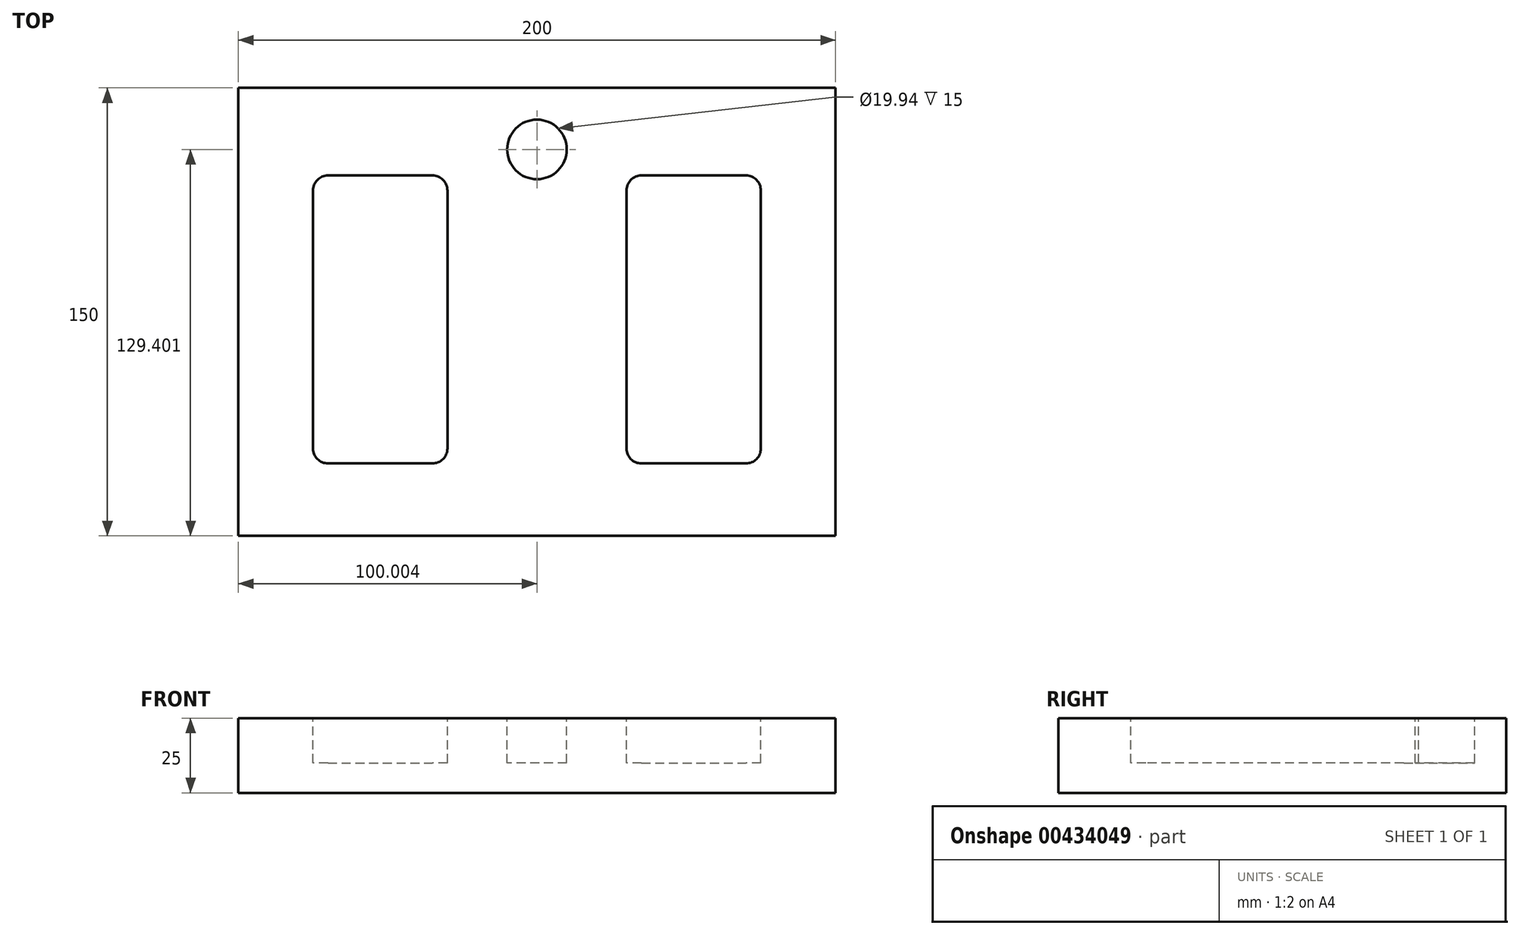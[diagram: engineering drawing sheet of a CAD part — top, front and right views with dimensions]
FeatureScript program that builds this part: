
annotation { "Feature Type Name" : "Feature", "Feature Type Description" : "" }
export const myFeature = defineFeature(function(context is Context, id is Id, definition is map)
    precondition{}
    {
        {
            var Q0;
            Q0=qCreatedBy(makeId("Top.planeOp"),FACE);
            var sketch = newSketch(context, id + "F0", { "sketchPlane" : qUnion([Q0])});
            skLineSegment(sketch, "E0.bottom", {"start": v(-75.08, 74.74) * mm, "end": v(124.92, 74.74) * mm});
            skLineSegment(sketch, "E0.top", {"start": v(-75.08, -75.26) * mm, "end": v(124.92, -75.26) * mm});
            skLineSegment(sketch, "E0.left", {"start": v(-75.08, 74.74) * mm, "end": v(-75.08, -75.26) * mm});
            skLineSegment(sketch, "E0.right", {"start": v(124.92, 74.74) * mm, "end": v(124.92, -75.26) * mm});
            skSolve(sketch);
        }
        {
            var Q0;
            Q0 = qSketchRegion(id + "F0", true);
            extrude(context, id + "F1", {"entities" : qUnion([Q0]), "depth" : 25 * mm});
        }
        {
            var Q0;
            Q0=makeQuery(id+"F1.opExtrude","CAP_FACE",FACE,{"disambiguationData":[OSD([sQuery(id+"F0.wireOp",EDGE,"E0.bottom"),sQuery(id+"F0.wireOp",EDGE,"E0.top"),sQuery(id+"F0.wireOp",EDGE,"E0.left"),sQuery(id+"F0.wireOp",EDGE,"E0.right")])],"isStart":false});
            var sketch = newSketch(context, id + "F2", { "sketchPlane" : qUnion([Q0])});
            skCircle(sketch, "E1", {"center": v(24.92, 54.14) * mm, "radius": 9.97 * mm});
            skSolve(sketch);
        }
        {
            var Q0;
            Q0 = qSketchRegion(id + "F2", true);
            extrude(context, id + "F3", {"entities" : qUnion([Q0]), "operationType" : NewBodyOperationType.REMOVE, "oppositeDirection" : true, "depth" : 15 * mm});
        }
        {
            var Q0;
            Q0=makeQuery(id+"F1.opExtrude","CAP_FACE",FACE,{"disambiguationData":[OSD([sQuery(id+"F0.wireOp",EDGE,"E0.bottom"),sQuery(id+"F0.wireOp",EDGE,"E0.top"),sQuery(id+"F0.wireOp",EDGE,"E0.left"),sQuery(id+"F0.wireOp",EDGE,"E0.right")])],"isStart":false});
            var sketch = newSketch(context, id + "F4", { "sketchPlane" : qUnion([Q0])});
            skLineSegment(sketch, "E2.bottom", {"start": v(-45.08, 45.42) * mm, "end": v(-10.08, 45.42) * mm});
            skLineSegment(sketch, "E2.top", {"start": v(-45.08, -50.99) * mm, "end": v(-10.08, -50.99) * mm});
            skLineSegment(sketch, "E2.left", {"start": v(-50.08, 40.42) * mm, "end": v(-50.08, -45.99) * mm});
            skLineSegment(sketch, "E2.right", {"start": v(-5.08, 40.42) * mm, "end": v(-5.08, -45.99) * mm});
            skLineSegment(sketch, "E3.bottom", {"start": v(59.92, 45.42) * mm, "end": v(94.92, 45.42) * mm});
            skLineSegment(sketch, "E3.top", {"start": v(59.92, -50.99) * mm, "end": v(94.92, -50.99) * mm});
            skLineSegment(sketch, "E3.left", {"start": v(54.92, 40.42) * mm, "end": v(54.92, -45.99) * mm});
            skLineSegment(sketch, "E3.right", {"start": v(99.92, 40.42) * mm, "end": v(99.92, -45.99) * mm});
            skPoint(sketch, "E4.visualSharp", {"position": v(-50.08, 45.42) * mm});
            skArc(sketch, "E4.filletArc", {"start": v(-45.08, 45.42) * mm, "mid": v(-48.61, 43.95) * mm, "end": v(-50.08, 40.42) * mm});
            skPoint(sketch, "E5.visualSharp", {"position": v(-5.08, 45.42) * mm});
            skArc(sketch, "E5.filletArc", {"start": v(-5.08, 40.42) * mm, "mid": v(-6.54, 43.95) * mm, "end": v(-10.08, 45.42) * mm});
            skPoint(sketch, "E6.visualSharp", {"position": v(-5.08, -50.99) * mm});
            skArc(sketch, "E6.filletArc", {"start": v(-10.08, -50.99) * mm, "mid": v(-6.54, -49.52) * mm, "end": v(-5.08, -45.99) * mm});
            skPoint(sketch, "E7.visualSharp", {"position": v(-50.08, -50.99) * mm});
            skArc(sketch, "E7.filletArc", {"start": v(-50.08, -45.99) * mm, "mid": v(-48.61, -49.52) * mm, "end": v(-45.08, -50.99) * mm});
            skPoint(sketch, "E8.visualSharp", {"position": v(54.92, 45.42) * mm});
            skArc(sketch, "E8.filletArc", {"start": v(59.92, 45.42) * mm, "mid": v(56.39, 43.95) * mm, "end": v(54.92, 40.42) * mm});
            skPoint(sketch, "E9.visualSharp", {"position": v(99.92, 45.42) * mm});
            skArc(sketch, "E9.filletArc", {"start": v(99.92, 40.42) * mm, "mid": v(98.46, 43.95) * mm, "end": v(94.92, 45.42) * mm});
            skPoint(sketch, "E10.visualSharp", {"position": v(99.92, -50.99) * mm});
            skArc(sketch, "E10.filletArc", {"start": v(94.92, -50.99) * mm, "mid": v(98.46, -49.52) * mm, "end": v(99.92, -45.99) * mm});
            skPoint(sketch, "E11.visualSharp", {"position": v(54.92, -50.99) * mm});
            skArc(sketch, "E11.filletArc", {"start": v(54.92, -45.99) * mm, "mid": v(56.39, -49.52) * mm, "end": v(59.92, -50.99) * mm});
            skSolve(sketch);
        }
        {
            var Q0;
            Q0 = qSketchRegion(id + "F4", true);
            extrude(context, id + "F5", {"entities" : qUnion([Q0]), "operationType" : NewBodyOperationType.REMOVE, "oppositeDirection" : true, "depth" : 15 * mm});
        }
    });
